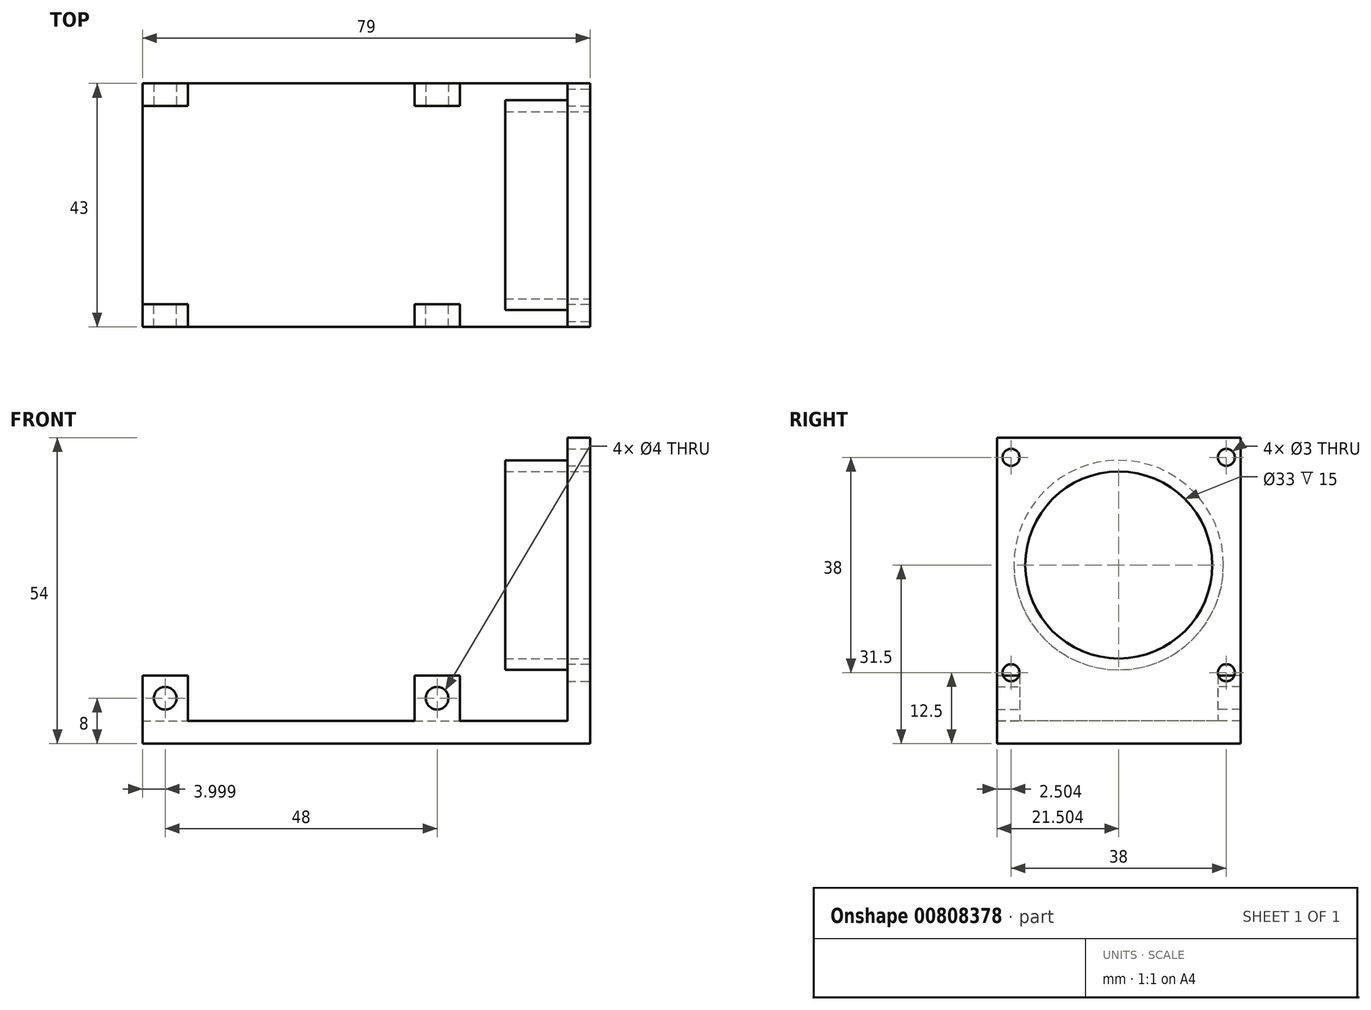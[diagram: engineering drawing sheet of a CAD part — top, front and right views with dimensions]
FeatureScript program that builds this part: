
annotation { "Feature Type Name" : "Feature", "Feature Type Description" : "" }
export const myFeature = defineFeature(function(context is Context, id is Id, definition is map)
    precondition{}
    {
        {
            var Q0;
            Q0=qCreatedBy(makeId("Top.planeOp"),FACE);
            var sketch = newSketch(context, id + "F0", { "sketchPlane" : qUnion([Q0])});
            skLineSegment(sketch, "E0.bottom", {"start": v(-31, 17.68) * mm, "end": v(48, 17.68) * mm});
            skLineSegment(sketch, "E0.top", {"start": v(-31, -25.32) * mm, "end": v(48, -25.32) * mm});
            skLineSegment(sketch, "E0.left", {"start": v(-31, 17.68) * mm, "end": v(-31, -25.32) * mm});
            skLineSegment(sketch, "E0.right", {"start": v(48, 17.68) * mm, "end": v(48, -25.32) * mm});
            skSolve(sketch);
        }
        {
            var Q0;
            Q0=makeQuery(id+"F0.imprint","IMPRINT",FACE,{"disambiguationData":[TD([[makeQuery(id+"F0.imprint","IMPRINT",EDGE,{"derivedFrom":sQuery(id+"F0.wireOp",EDGE,"E0.bottom")}),-1.0]])]});
            extrude(context, id + "F1", {"entities" : qUnion([Q0]), "depth" : 4 * mm, "offsetDistance" : 25 * mm});
        }
        {
            var Q0;
            Q0=makeQuery(id+"F1.opExtrude","CAP_FACE",FACE,{"disambiguationData":[OSD([sQuery(id+"F0.wireOp",EDGE,"E0.bottom"),sQuery(id+"F0.wireOp",EDGE,"E0.top"),sQuery(id+"F0.wireOp",EDGE,"E0.left"),sQuery(id+"F0.wireOp",EDGE,"E0.right")])],"isStart":false});
            var sketch = newSketch(context, id + "F2", { "sketchPlane" : qUnion([Q0])});
            skLineSegment(sketch, "E1.bottom", {"start": v(48, 17.68) * mm, "end": v(44, 17.68) * mm});
            skLineSegment(sketch, "E1.top", {"start": v(48, -25.32) * mm, "end": v(44, -25.32) * mm});
            skLineSegment(sketch, "E1.left", {"start": v(48, 17.68) * mm, "end": v(48, -25.32) * mm});
            skLineSegment(sketch, "E1.right", {"start": v(44, 17.68) * mm, "end": v(44, -25.32) * mm});
            skSolve(sketch);
        }
        {
            var Q0;
            Q0=makeQuery(id+"F2.imprint","IMPRINT",FACE,{"disambiguationData":[TD([[makeQuery(id+"F2.imprint","IMPRINT",EDGE,{"derivedFrom":sQuery(id+"F2.wireOp",EDGE,"E1.bottom")}),-1.0]])]});
            extrude(context, id + "F3", {"entities" : qUnion([Q0]), "operationType" : NewBodyOperationType.ADD, "depth" : 50 * mm, "offsetDistance" : 25 * mm});
        }
        {
            var Q0;
            Q0=makeQuery(id+"F1.opExtrude","CAP_FACE",FACE,{"disambiguationData":[OSD([sQuery(id+"F0.wireOp",EDGE,"E0.bottom"),sQuery(id+"F0.wireOp",EDGE,"E0.top"),sQuery(id+"F0.wireOp",EDGE,"E0.left"),sQuery(id+"F0.wireOp",EDGE,"E0.right")])],"isStart":false});
            var sketch = newSketch(context, id + "F4", { "sketchPlane" : qUnion([Q0])});
            skLineSegment(sketch, "E2.bottom", {"start": v(-31, -25.32) * mm, "end": v(-23, -25.32) * mm});
            skLineSegment(sketch, "E2.top", {"start": v(-31, -21.32) * mm, "end": v(-23, -21.32) * mm});
            skLineSegment(sketch, "E2.left", {"start": v(-31, -25.32) * mm, "end": v(-31, -21.32) * mm});
            skLineSegment(sketch, "E2.right", {"start": v(-23, -25.32) * mm, "end": v(-23, -21.32) * mm});
            skSolve(sketch);
        }
        {
            var Q0;
            Q0 = qSketchRegion(id + "F4", true);
            extrude(context, id + "F5", {"entities" : qUnion([Q0]), "operationType" : NewBodyOperationType.ADD, "depth" : 8 * mm, "offsetDistance" : 25 * mm});
        }
        {
            var Q0;
            Q0=makeQuery(id+"F1.opExtrude","CAP_FACE",FACE,{"disambiguationData":[OSD([sQuery(id+"F0.wireOp",EDGE,"E0.bottom"),sQuery(id+"F0.wireOp",EDGE,"E0.top"),sQuery(id+"F0.wireOp",EDGE,"E0.left"),sQuery(id+"F0.wireOp",EDGE,"E0.right")])],"isStart":false});
            var sketch = newSketch(context, id + "F6", { "sketchPlane" : qUnion([Q0])});
            skLineSegment(sketch, "E3.bottom", {"start": v(-31, 17.68) * mm, "end": v(-23, 17.68) * mm});
            skLineSegment(sketch, "E3.top", {"start": v(-31, 13.68) * mm, "end": v(-23, 13.68) * mm});
            skLineSegment(sketch, "E3.left", {"start": v(-31, 17.68) * mm, "end": v(-31, 13.68) * mm});
            skLineSegment(sketch, "E3.right", {"start": v(-23, 17.68) * mm, "end": v(-23, 13.68) * mm});
            skSolve(sketch);
        }
        {
            var Q0;
            Q0=makeQuery(id+"F6.imprint","IMPRINT",FACE,{"disambiguationData":[TD([[makeQuery(id+"F6.imprint","IMPRINT",EDGE,{"derivedFrom":sQuery(id+"F6.wireOp",EDGE,"E3.bottom")}),-1.0]])]});
            extrude(context, id + "F7", {"entities" : qUnion([Q0]), "operationType" : NewBodyOperationType.ADD, "depth" : 8 * mm, "offsetDistance" : 25 * mm});
        }
        {
            var Q0;
            Q0=makeQuery(id+"F1.opExtrude","CAP_FACE",FACE,{"disambiguationData":[OSD([sQuery(id+"F0.wireOp",EDGE,"E0.bottom"),sQuery(id+"F0.wireOp",EDGE,"E0.top"),sQuery(id+"F0.wireOp",EDGE,"E0.left"),sQuery(id+"F0.wireOp",EDGE,"E0.right")])],"isStart":false});
            var sketch = newSketch(context, id + "F8", { "sketchPlane" : qUnion([Q0])});
            skLineSegment(sketch, "E4.bottom", {"start": v(17, 17.68) * mm, "end": v(25, 17.68) * mm});
            skLineSegment(sketch, "E4.top", {"start": v(17, 13.68) * mm, "end": v(25, 13.68) * mm});
            skLineSegment(sketch, "E4.left", {"start": v(17, 17.68) * mm, "end": v(17, 13.68) * mm});
            skLineSegment(sketch, "E4.right", {"start": v(25, 17.68) * mm, "end": v(25, 13.68) * mm});
            skSolve(sketch);
        }
        {
            var Q0;
            Q0=makeQuery(id+"F8.imprint","IMPRINT",FACE,{"disambiguationData":[TD([[makeQuery(id+"F8.imprint","IMPRINT",EDGE,{"derivedFrom":sQuery(id+"F8.wireOp",EDGE,"E4.bottom")}),-1.0]])]});
            extrude(context, id + "F9", {"entities" : qUnion([Q0]), "operationType" : NewBodyOperationType.ADD, "depth" : 8 * mm, "offsetDistance" : 25 * mm});
        }
        {
            var Q0;
            Q0=makeQuery(id+"F1.opExtrude","CAP_FACE",FACE,{"disambiguationData":[OSD([sQuery(id+"F0.wireOp",EDGE,"E0.bottom"),sQuery(id+"F0.wireOp",EDGE,"E0.top"),sQuery(id+"F0.wireOp",EDGE,"E0.left"),sQuery(id+"F0.wireOp",EDGE,"E0.right")])],"isStart":false});
            var sketch = newSketch(context, id + "F10", { "sketchPlane" : qUnion([Q0])});
            skLineSegment(sketch, "E5.bottom", {"start": v(17, -25.32) * mm, "end": v(25, -25.32) * mm});
            skLineSegment(sketch, "E5.top", {"start": v(17, -21.32) * mm, "end": v(25, -21.32) * mm});
            skLineSegment(sketch, "E5.left", {"start": v(17, -25.32) * mm, "end": v(17, -21.32) * mm});
            skLineSegment(sketch, "E5.right", {"start": v(25, -25.32) * mm, "end": v(25, -21.32) * mm});
            skSolve(sketch);
        }
        {
            var Q0;
            Q0=makeQuery(id+"F10.imprint","IMPRINT",FACE,{"disambiguationData":[TD([[makeQuery(id+"F10.imprint","IMPRINT",EDGE,{"derivedFrom":sQuery(id+"F10.wireOp",EDGE,"E5.bottom")}),1.0]])]});
            extrude(context, id + "F11", {"entities" : qUnion([Q0]), "operationType" : NewBodyOperationType.ADD, "depth" : 8 * mm, "offsetDistance" : 25 * mm});
        }
        {
            var Q0;
            Q0=makeQuery(id+"F7.opExtrude","SWEPT_FACE",FACE,{"disambiguationData":[OSD([sQuery(id+"F6.wireOp",EDGE,"E3.top")])]});
            var sketch = newSketch(context, id + "F12", { "sketchPlane" : qUnion([Q0])});
            skPoint(sketch, "E6", {"position": v(-27, 8) * mm});
            skPoint(sketch, "E6.positionSnap0", {"position": v(-27, 12) * mm});
            skSolve(sketch);
        }
        {
            var Q0;
            Q0=sQuery(id+"F12.wireOp",VERTEX,"E6");
            var Q1;
            Q1=makeQuery(id+"F1.opExtrude","SWEPT_BODY",BODY,{"disambiguationData":[OSD([sQuery(id+"F0.wireOp",EDGE,"E0.bottom"),sQuery(id+"F0.wireOp",EDGE,"E0.top"),sQuery(id+"F0.wireOp",EDGE,"E0.left"),sQuery(id+"F0.wireOp",EDGE,"E0.right")])]});
            hole(context, id + "F13", {"style" : HoleStyle.SIMPLE, "endStyle" : HoleEndStyle.THROUGH, "holeDiameter" : 4 * mm, "majorDiameter" : 5 * mm, "isTappedThrough" : true, "tappedDepth" : 12 * mm, "tapClearance" : 3, "locations" : qUnion([Q0]), "scope" : qUnion([Q1])});
        }
        {
            var Q0;
            Q0=makeQuery(id+"F9.opExtrude","SWEPT_FACE",FACE,{"disambiguationData":[OSD([sQuery(id+"F8.wireOp",EDGE,"E4.top")])]});
            var sketch = newSketch(context, id + "F14", { "sketchPlane" : qUnion([Q0])});
            skPoint(sketch, "E7", {"position": v(21, 8) * mm});
            skPoint(sketch, "E7.positionSnap0", {"position": v(21, 12) * mm});
            skSolve(sketch);
        }
        {
            var Q0;
            Q0=sQuery(id+"F14.wireOp",VERTEX,"E7");
            var Q1;
            Q1=makeQuery(id+"F1.opExtrude","SWEPT_BODY",BODY,{"disambiguationData":[OSD([sQuery(id+"F0.wireOp",EDGE,"E0.bottom"),sQuery(id+"F0.wireOp",EDGE,"E0.top"),sQuery(id+"F0.wireOp",EDGE,"E0.left"),sQuery(id+"F0.wireOp",EDGE,"E0.right")])]});
            hole(context, id + "F15", {"style" : HoleStyle.SIMPLE, "endStyle" : HoleEndStyle.THROUGH, "holeDiameter" : 4 * mm, "majorDiameter" : 5 * mm, "isTappedThrough" : true, "tappedDepth" : 12 * mm, "tapClearance" : 3, "locations" : qUnion([Q0]), "scope" : qUnion([Q1])});
        }
        {
            var Q0;
            Q0=makeQuery(id+"F5.opExtrude","SWEPT_FACE",FACE,{"disambiguationData":[OSD([sQuery(id+"F4.wireOp",EDGE,"E2.top")])]});
            var sketch = newSketch(context, id + "F16", { "sketchPlane" : qUnion([Q0])});
            skPoint(sketch, "E8", {"position": v(27, 8) * mm});
            skPoint(sketch, "E8.positionSnap0", {"position": v(27, 12) * mm});
            skSolve(sketch);
        }
        {
            var Q0;
            Q0=sQuery(id+"F16.wireOp",VERTEX,"E8");
            var Q1;
            Q1=makeQuery(id+"F1.opExtrude","SWEPT_BODY",BODY,{"disambiguationData":[OSD([sQuery(id+"F0.wireOp",EDGE,"E0.bottom"),sQuery(id+"F0.wireOp",EDGE,"E0.top"),sQuery(id+"F0.wireOp",EDGE,"E0.left"),sQuery(id+"F0.wireOp",EDGE,"E0.right")])]});
            hole(context, id + "F17", {"style" : HoleStyle.SIMPLE, "endStyle" : HoleEndStyle.THROUGH, "holeDiameter" : 4 * mm, "majorDiameter" : 5 * mm, "isTappedThrough" : true, "tappedDepth" : 12 * mm, "tapClearance" : 3, "locations" : qUnion([Q0]), "scope" : qUnion([Q1])});
        }
        {
            var Q0;
            Q0=makeQuery(id+"F11.opExtrude","SWEPT_FACE",FACE,{"disambiguationData":[OSD([sQuery(id+"F10.wireOp",EDGE,"E5.top")])]});
            var sketch = newSketch(context, id + "F18", { "sketchPlane" : qUnion([Q0])});
            skPoint(sketch, "E9", {"position": v(-21, 8) * mm});
            skPoint(sketch, "E9.positionSnap0", {"position": v(-21, 12) * mm});
            skPoint(sketch, "E9.positionSnap1", {"position": v(-17, 8) * mm});
            skSolve(sketch);
        }
        {
            var Q0;
            Q0=sQuery(id+"F18.wireOp",VERTEX,"E9");
            var Q1;
            Q1=makeQuery(id+"F1.opExtrude","SWEPT_BODY",BODY,{"disambiguationData":[OSD([sQuery(id+"F0.wireOp",EDGE,"E0.bottom"),sQuery(id+"F0.wireOp",EDGE,"E0.top"),sQuery(id+"F0.wireOp",EDGE,"E0.left"),sQuery(id+"F0.wireOp",EDGE,"E0.right")])]});
            hole(context, id + "F19", {"style" : HoleStyle.SIMPLE, "endStyle" : HoleEndStyle.THROUGH, "holeDiameter" : 4 * mm, "majorDiameter" : 5 * mm, "isTappedThrough" : true, "tappedDepth" : 12 * mm, "tapClearance" : 3, "locations" : qUnion([Q0]), "scope" : qUnion([Q1])});
        }
        {
            var Q0;
            Q0=makeQuery(id+"F3.boolean.opBoolean","MERGE",FACE,{"derivedFrom":[makeQuery(id+"F1.opExtrude","SWEPT_FACE",FACE,{"disambiguationData":[OSD([sQuery(id+"F0.wireOp",EDGE,"E0.right")])]}),makeQuery(id+"F3.opExtrude","SWEPT_FACE",FACE,{"disambiguationData":[OSD([sQuery(id+"F2.wireOp",EDGE,"E1.left")])]})]});
            var sketch = newSketch(context, id + "F20", { "sketchPlane" : qUnion([Q0])});
            skPoint(sketch, "E10", {"position": v(-3.82, 31.5) * mm});
            skPoint(sketch, "E10.positionSnap0", {"position": v(-3.82, 54) * mm});
            skSolve(sketch);
        }
        {
            var Q0;
            Q0=sQuery(id+"F20.wireOp",VERTEX,"E10");
            var Q1;
            Q1=makeQuery(id+"F1.opExtrude","SWEPT_BODY",BODY,{"disambiguationData":[OSD([sQuery(id+"F0.wireOp",EDGE,"E0.bottom"),sQuery(id+"F0.wireOp",EDGE,"E0.top"),sQuery(id+"F0.wireOp",EDGE,"E0.left"),sQuery(id+"F0.wireOp",EDGE,"E0.right")])]});
            hole(context, id + "F21", {"style" : HoleStyle.SIMPLE, "endStyle" : HoleEndStyle.THROUGH, "holeDiameter" : 33 * mm, "majorDiameter" : 5 * mm, "isTappedThrough" : true, "tappedDepth" : 12 * mm, "tapClearance" : 3, "locations" : qUnion([Q0]), "scope" : qUnion([Q1])});
        }
        {
            var Q0;
            Q0=makeQuery(id+"F3.opExtrude","SWEPT_FACE",FACE,{"disambiguationData":[OSD([sQuery(id+"F2.wireOp",EDGE,"E1.right")])]});
            var sketch = newSketch(context, id + "F22", { "sketchPlane" : qUnion([Q0])});
            skCircle(sketch, "E11", {"center": v(3.82, 31.5) * mm, "radius": 18.5 * mm});
            skSolve(sketch);
        }
        {
            var Q0;
            Q0=makeQuery(id+"F22.imprint","IMPRINT",FACE,{"disambiguationData":[TD([[makeQuery(id+"F22.imprint","IMPRINT",EDGE,{"derivedFrom":sQuery(id+"F22.wireOp",EDGE,"E11")}),1.0]])]});
            extrude(context, id + "F23", {"entities" : qUnion([Q0]), "operationType" : NewBodyOperationType.ADD, "depth" : 11 * mm, "offsetDistance" : 25 * mm});
        }
        {
            var Q0;
            Q0=makeQuery(id+"F3.boolean.opBoolean","MERGE",FACE,{"derivedFrom":[makeQuery(id+"F1.opExtrude","SWEPT_FACE",FACE,{"disambiguationData":[OSD([sQuery(id+"F0.wireOp",EDGE,"E0.right")])]}),makeQuery(id+"F3.opExtrude","SWEPT_FACE",FACE,{"disambiguationData":[OSD([sQuery(id+"F2.wireOp",EDGE,"E1.left")])]})]});
            var sketch = newSketch(context, id + "F24", { "sketchPlane" : qUnion([Q0])});
            skPoint(sketch, "E12", {"position": v(-22.82, 50.5) * mm});
            skSolve(sketch);
        }
        {
            var Q0;
            Q0=sQuery(id+"F24.wireOp",VERTEX,"E12");
            var Q1;
            Q1=makeQuery(id+"F1.opExtrude","SWEPT_BODY",BODY,{"disambiguationData":[OSD([sQuery(id+"F0.wireOp",EDGE,"E0.bottom"),sQuery(id+"F0.wireOp",EDGE,"E0.top"),sQuery(id+"F0.wireOp",EDGE,"E0.left"),sQuery(id+"F0.wireOp",EDGE,"E0.right")])]});
            hole(context, id + "F25", {"style" : HoleStyle.SIMPLE, "endStyle" : HoleEndStyle.THROUGH, "holeDiameter" : 3 * mm, "majorDiameter" : 5 * mm, "isTappedThrough" : true, "tappedDepth" : 12 * mm, "tapClearance" : 3, "locations" : qUnion([Q0]), "scope" : qUnion([Q1])});
        }
        {
            var Q0;
            Q0=makeQuery(id+"F3.boolean.opBoolean","MERGE",FACE,{"derivedFrom":[makeQuery(id+"F1.opExtrude","SWEPT_FACE",FACE,{"disambiguationData":[OSD([sQuery(id+"F0.wireOp",EDGE,"E0.right")])]}),makeQuery(id+"F3.opExtrude","SWEPT_FACE",FACE,{"disambiguationData":[OSD([sQuery(id+"F2.wireOp",EDGE,"E1.left")])]})]});
            var sketch = newSketch(context, id + "F26", { "sketchPlane" : qUnion([Q0])});
            skPoint(sketch, "E13", {"position": v(15.18, 50.5) * mm});
            skSolve(sketch);
        }
        {
            var Q0;
            Q0=sQuery(id+"F26.wireOp",VERTEX,"E13");
            var Q1;
            Q1=makeQuery(id+"F1.opExtrude","SWEPT_BODY",BODY,{"disambiguationData":[OSD([sQuery(id+"F0.wireOp",EDGE,"E0.bottom"),sQuery(id+"F0.wireOp",EDGE,"E0.top"),sQuery(id+"F0.wireOp",EDGE,"E0.left"),sQuery(id+"F0.wireOp",EDGE,"E0.right")])]});
            hole(context, id + "F27", {"style" : HoleStyle.SIMPLE, "endStyle" : HoleEndStyle.THROUGH, "holeDiameter" : 3 * mm, "majorDiameter" : 5 * mm, "isTappedThrough" : true, "tappedDepth" : 12 * mm, "tapClearance" : 3, "locations" : qUnion([Q0]), "scope" : qUnion([Q1])});
        }
        {
            var Q0;
            Q0=makeQuery(id+"F3.boolean.opBoolean","MERGE",FACE,{"derivedFrom":[makeQuery(id+"F1.opExtrude","SWEPT_FACE",FACE,{"disambiguationData":[OSD([sQuery(id+"F0.wireOp",EDGE,"E0.right")])]}),makeQuery(id+"F3.opExtrude","SWEPT_FACE",FACE,{"disambiguationData":[OSD([sQuery(id+"F2.wireOp",EDGE,"E1.left")])]})]});
            var sketch = newSketch(context, id + "F28", { "sketchPlane" : qUnion([Q0])});
            skPoint(sketch, "E14", {"position": v(-22.82, 12.5) * mm});
            skSolve(sketch);
        }
        {
            var Q0;
            Q0=sQuery(id+"F28.wireOp",VERTEX,"E14");
            var Q1;
            Q1=makeQuery(id+"F1.opExtrude","SWEPT_BODY",BODY,{"disambiguationData":[OSD([sQuery(id+"F0.wireOp",EDGE,"E0.bottom"),sQuery(id+"F0.wireOp",EDGE,"E0.top"),sQuery(id+"F0.wireOp",EDGE,"E0.left"),sQuery(id+"F0.wireOp",EDGE,"E0.right")])]});
            hole(context, id + "F29", {"style" : HoleStyle.SIMPLE, "endStyle" : HoleEndStyle.BLIND, "holeDiameter" : 3 * mm, "majorDiameter" : 5 * mm, "holeDepth" : 12 * mm, "isTappedThrough" : true, "tappedDepth" : 12 * mm, "tapClearance" : 3, "locations" : qUnion([Q0]), "scope" : qUnion([Q1])});
        }
        {
            var Q0;
            Q0=makeQuery(id+"F3.boolean.opBoolean","MERGE",FACE,{"derivedFrom":[makeQuery(id+"F1.opExtrude","SWEPT_FACE",FACE,{"disambiguationData":[OSD([sQuery(id+"F0.wireOp",EDGE,"E0.right")])]}),makeQuery(id+"F3.opExtrude","SWEPT_FACE",FACE,{"disambiguationData":[OSD([sQuery(id+"F2.wireOp",EDGE,"E1.left")])]})]});
            var sketch = newSketch(context, id + "F30", { "sketchPlane" : qUnion([Q0])});
            skPoint(sketch, "E15", {"position": v(15.18, 12.5) * mm});
            skSolve(sketch);
        }
        {
            var Q0;
            Q0=sQuery(id+"F30.wireOp",VERTEX,"E15");
            var Q1;
            Q1=makeQuery(id+"F1.opExtrude","SWEPT_BODY",BODY,{"disambiguationData":[OSD([sQuery(id+"F0.wireOp",EDGE,"E0.bottom"),sQuery(id+"F0.wireOp",EDGE,"E0.top"),sQuery(id+"F0.wireOp",EDGE,"E0.left"),sQuery(id+"F0.wireOp",EDGE,"E0.right")])]});
            hole(context, id + "F31", {"style" : HoleStyle.SIMPLE, "endStyle" : HoleEndStyle.BLIND, "holeDiameter" : 3 * mm, "majorDiameter" : 5 * mm, "holeDepth" : 12 * mm, "isTappedThrough" : true, "tappedDepth" : 12 * mm, "tapClearance" : 3, "locations" : qUnion([Q0]), "scope" : qUnion([Q1])});
        }
    });
